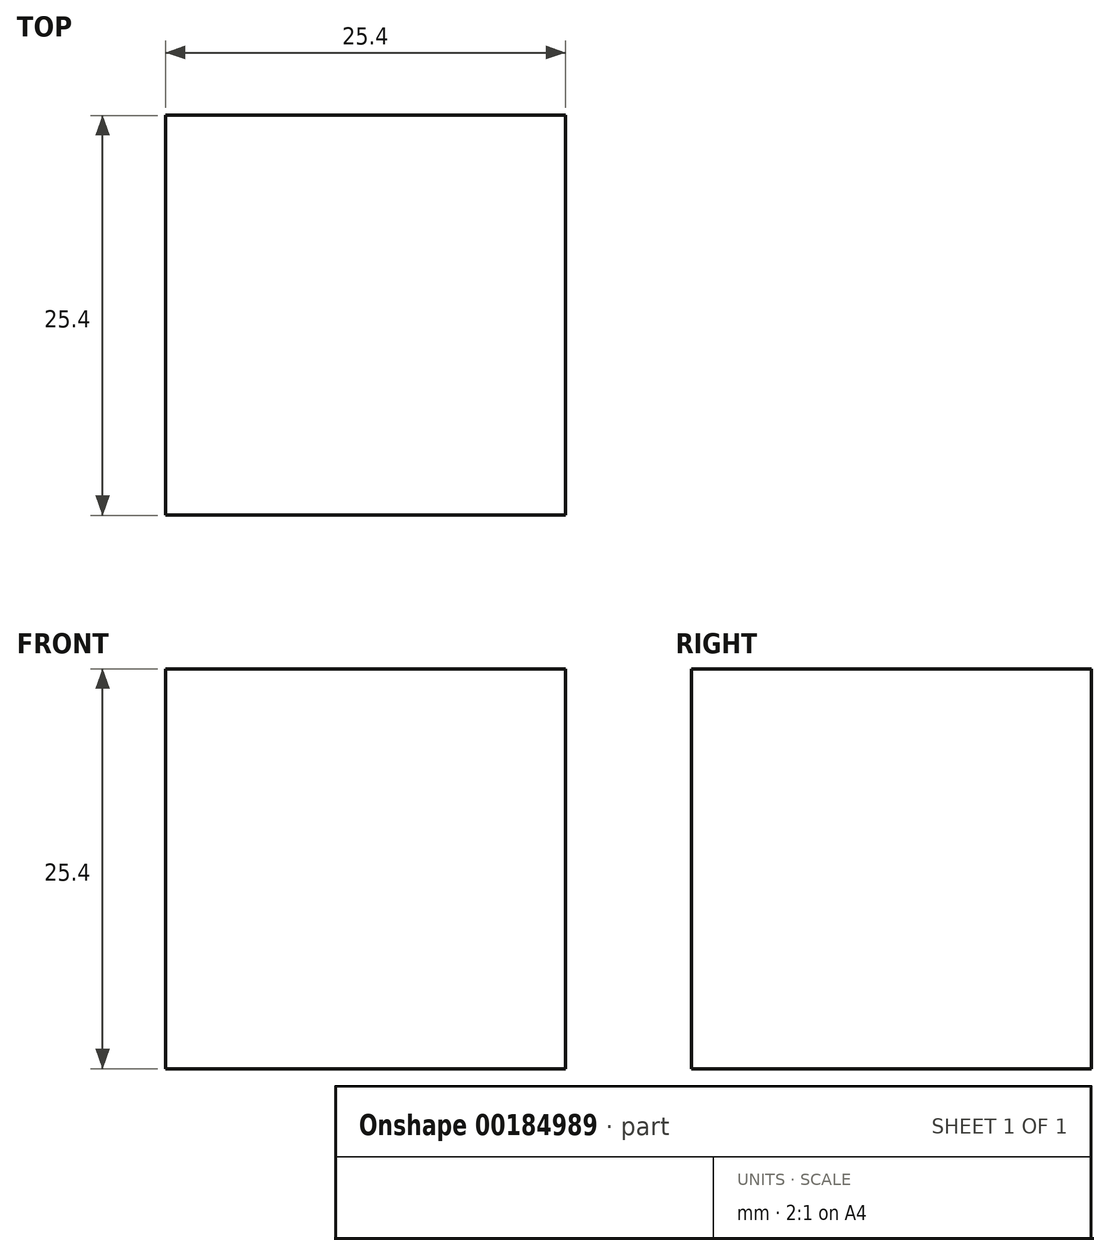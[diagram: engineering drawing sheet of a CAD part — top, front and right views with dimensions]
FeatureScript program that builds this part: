
annotation { "Feature Type Name" : "Feature", "Feature Type Description" : "" }
export const myFeature = defineFeature(function(context is Context, id is Id, definition is map)
    precondition{}
    {
        {
            var Q0;
            Q0=qCreatedBy(makeId("Top.planeOp"),FACE);
            var sketch = newSketch(context, id + "F0", { "sketchPlane" : qUnion([Q0])});
            skLineSegment(sketch, "E0.bottom", {"start": v(-13.49, 7.63) * mm, "end": v(11.91, 7.63) * mm});
            skLineSegment(sketch, "E0.top", {"start": v(-13.49, -17.77) * mm, "end": v(11.91, -17.77) * mm});
            skLineSegment(sketch, "E0.left", {"start": v(-13.49, 7.63) * mm, "end": v(-13.49, -17.77) * mm});
            skLineSegment(sketch, "E0.right", {"start": v(11.91, 7.63) * mm, "end": v(11.91, -17.77) * mm});
            skSolve(sketch);
        }
        {
            var Q0;
            Q0=makeQuery(id+"F0.imprint","IMPRINT",FACE,{"disambiguationData":[TD([[makeQuery(id+"F0.imprint","IMPRINT",EDGE,{"derivedFrom":sQuery(id+"F0.wireOp",EDGE,"E0.bottom")}),-1.0]])]});
            extrude(context, id + "F1", {"entities" : qUnion([Q0]), "depth" : 25.4 * mm});
        }
    });
